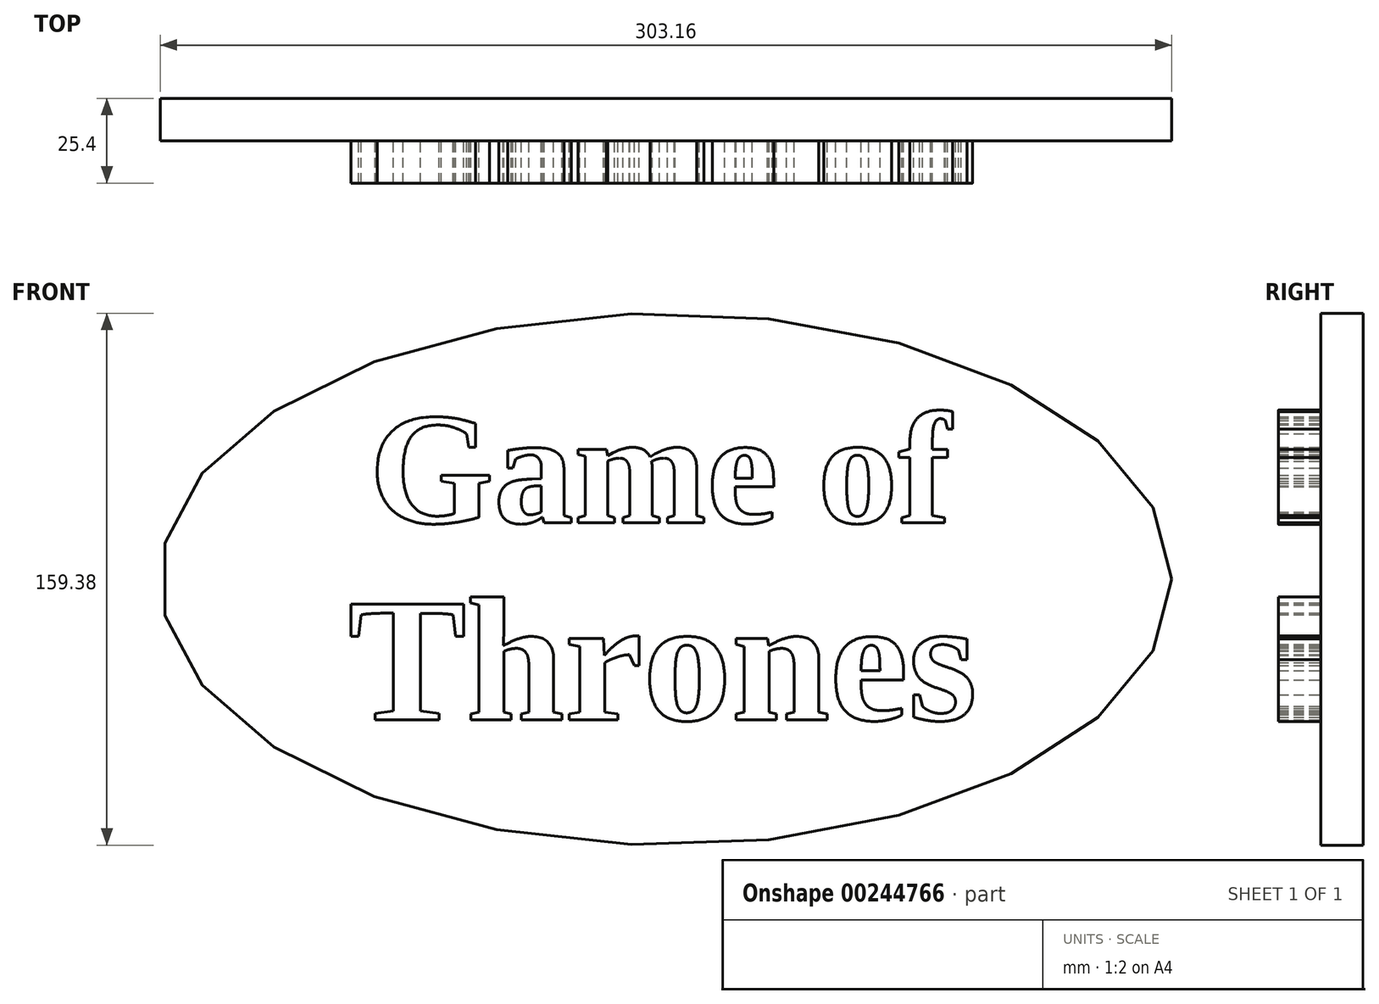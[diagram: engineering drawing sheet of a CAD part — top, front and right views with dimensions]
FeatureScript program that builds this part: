
annotation { "Feature Type Name" : "Feature", "Feature Type Description" : "" }
export const myFeature = defineFeature(function(context is Context, id is Id, definition is map)
    precondition{}
    {
        {
            var Q0;
            Q0=qCreatedBy(makeId("Front.planeOp"),FACE);
            var sketch = newSketch(context, id + "F0", { "sketchPlane" : qUnion([Q0])});
            skEllipse(sketch, "E0", {"center": v(0, 0) * mm, "majorRadius": 151.58 * mm, "minorRadius": 79.7 * mm, "majorAxis": v(1, 0)});
            skSolve(sketch);
        }
        {
            var Q0;
            Q0=qCreatedBy(makeId("Front.planeOp"),FACE);
            var sketch = newSketch(context, id + "F1", { "sketchPlane" : qUnion([Q0])});
            skText(sketch, "E1", { "text": "Game of", "fontName": "Tinos-Bold.ttf"});
            skText(sketch, "E2", { "text": "Thrones", "fontName": "Tinos-Bold.ttf"});
            const initialGuessF1  = {"E1": [-0.0889, 0.01693, 1, 0, 0.0345], "E2": [-0.09525, -0.04213, 1, 0, 0.03816]};
            skSetInitialGuess(sketch, initialGuessF1);
            skSolve(sketch);
        }
        {
            var Q0;
            Q0=makeQuery(id+"F0.imprint","IMPRINT",FACE,{"disambiguationData":[TD([[makeQuery(id+"F0.imprint","IMPRINT",EDGE,{"derivedFrom":sQuery(id+"F0.wireOp",EDGE,"E0")}),1.0]])]});
            extrude(context, id + "F2", {"entities" : qUnion([Q0]), "depth" : 12.7 * mm});
        }
        {
            var Q0;
            Q0 = qSketchRegion(id + "F1", true);
            extrude(context, id + "F3", {"entities" : qUnion([Q0]), "operationType" : NewBodyOperationType.ADD, "depth" : 25.4 * mm});
        }
    });
